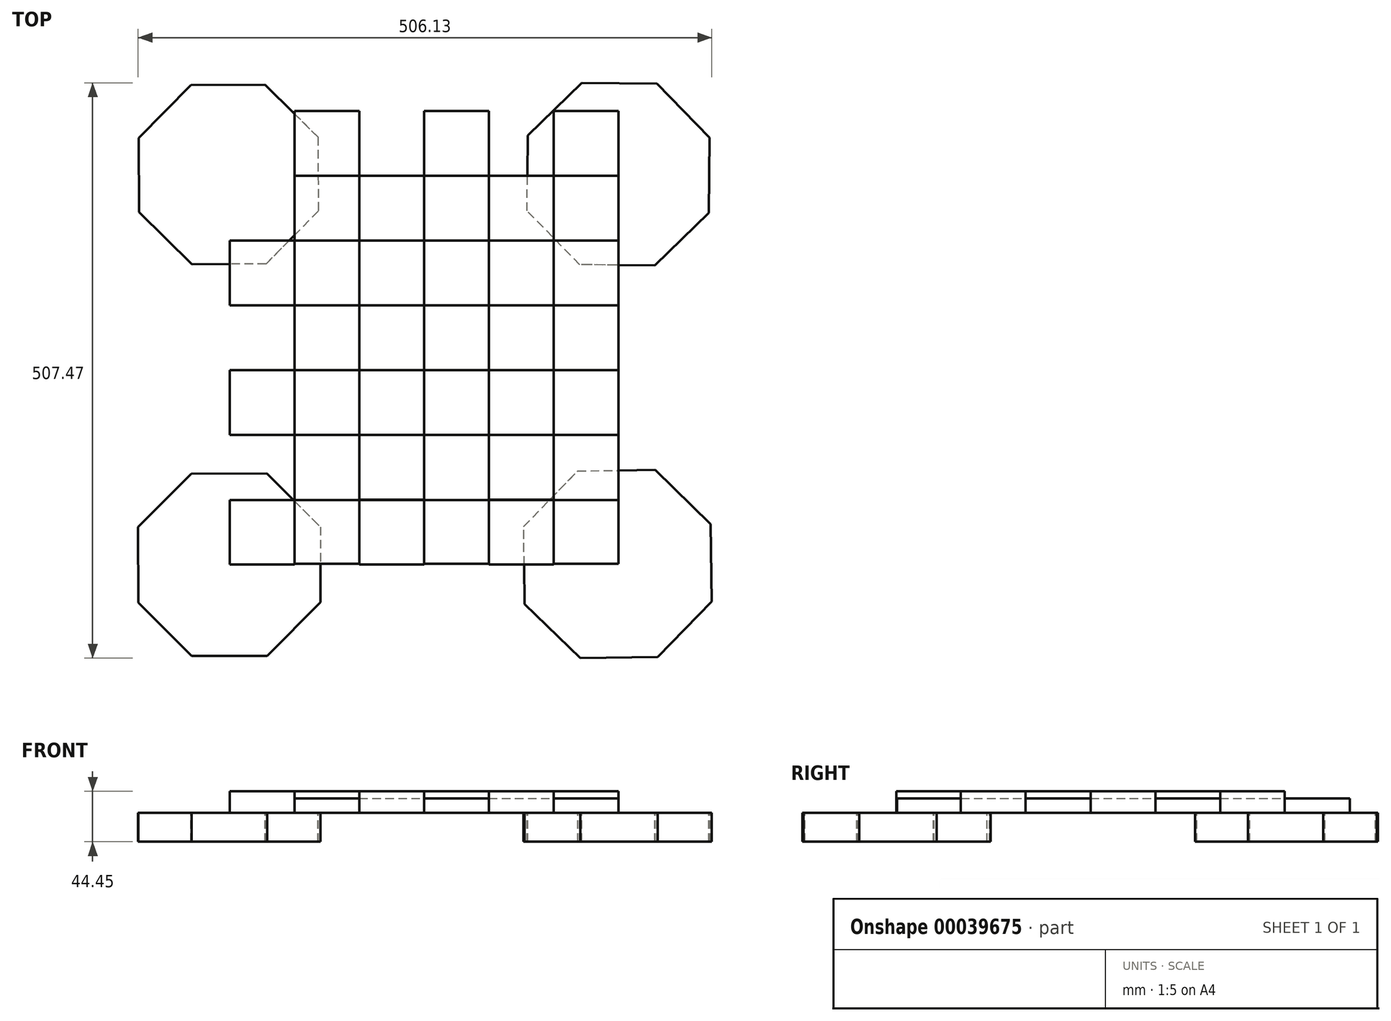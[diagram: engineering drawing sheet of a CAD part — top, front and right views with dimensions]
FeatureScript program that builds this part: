
annotation { "Feature Type Name" : "Feature", "Feature Type Description" : "" }
export const myFeature = defineFeature(function(context is Context, id is Id, definition is map)
    precondition{}
    {
        {
            var Q0;
            Q0=qCreatedBy(makeId("Top.planeOp"),FACE);
            var sketch = newSketch(context, id + "F0", { "sketchPlane" : qUnion([Q0])});
            skLineSegment(sketch, "E0.bottom", {"start": v(0, 0) * mm, "end": v(457.2, 0) * mm});
            skLineSegment(sketch, "E0.top", {"start": v(0, 457.2) * mm, "end": v(457.2, 457.2) * mm});
            skLineSegment(sketch, "E0.left", {"start": v(0, 0) * mm, "end": v(0, 457.2) * mm});
            skLineSegment(sketch, "E0.right", {"start": v(457.2, 0) * mm, "end": v(457.2, 457.2) * mm});
            skLineSegment(sketch, "E1.bottom", {"start": v(0, 457.2) * mm, "end": v(57.15, 457.2) * mm});
            skLineSegment(sketch, "E1.top", {"start": v(0, 0) * mm, "end": v(57.15, 0) * mm});
            skLineSegment(sketch, "E1.left", {"start": v(0, 457.2) * mm, "end": v(0, 0) * mm});
            skLineSegment(sketch, "E1.right", {"start": v(57.15, 457.2) * mm, "end": v(57.15, 0) * mm});
            skLineSegment(sketch, "E2.bottom", {"start": v(457.2, 457.2) * mm, "end": v(400.05, 457.2) * mm});
            skLineSegment(sketch, "E2.top", {"start": v(457.2, 0) * mm, "end": v(400.05, 0) * mm});
            skLineSegment(sketch, "E2.left", {"start": v(457.2, 457.2) * mm, "end": v(457.2, 0) * mm});
            skLineSegment(sketch, "E2.right", {"start": v(400.05, 457.2) * mm, "end": v(400.05, 0) * mm});
            skLineSegment(sketch, "E3.bottom", {"start": v(57.15, 0) * mm, "end": v(114.3, 0) * mm});
            skLineSegment(sketch, "E3.top", {"start": v(57.15, 457.2) * mm, "end": v(114.3, 457.2) * mm});
            skLineSegment(sketch, "E3.left", {"start": v(57.15, 0) * mm, "end": v(57.15, 457.2) * mm});
            skLineSegment(sketch, "E3.right", {"start": v(114.3, 0) * mm, "end": v(114.3, 457.2) * mm});
            skLineSegment(sketch, "E4.bottom", {"start": v(114.3, 0) * mm, "end": v(171.45, 0) * mm});
            skLineSegment(sketch, "E4.top", {"start": v(114.3, 457.2) * mm, "end": v(171.45, 457.2) * mm});
            skLineSegment(sketch, "E4.right", {"start": v(171.45, 0) * mm, "end": v(171.45, 457.2) * mm});
            skLineSegment(sketch, "E5.bottom", {"start": v(171.45, 0) * mm, "end": v(228.6, 0) * mm});
            skLineSegment(sketch, "E5.top", {"start": v(171.45, 457.2) * mm, "end": v(228.6, 457.2) * mm});
            skLineSegment(sketch, "E5.right", {"start": v(228.6, 0) * mm, "end": v(228.6, 457.2) * mm});
            skLineSegment(sketch, "E6.bottom", {"start": v(228.6, 0) * mm, "end": v(285.75, 0) * mm});
            skLineSegment(sketch, "E6.top", {"start": v(228.6, 457.2) * mm, "end": v(285.75, 457.2) * mm});
            skLineSegment(sketch, "E6.right", {"start": v(285.75, 0) * mm, "end": v(285.75, 457.2) * mm});
            skLineSegment(sketch, "E7.bottom", {"start": v(285.75, 0) * mm, "end": v(342.9, 0) * mm});
            skLineSegment(sketch, "E7.top", {"start": v(285.75, 457.2) * mm, "end": v(342.9, 457.2) * mm});
            skLineSegment(sketch, "E7.right", {"start": v(342.9, 0) * mm, "end": v(342.9, 457.2) * mm});
            skLineSegment(sketch, "E8.top", {"start": v(0, 400.05) * mm, "end": v(457.2, 400.05) * mm});
            skLineSegment(sketch, "E8.left", {"start": v(0, 457.2) * mm, "end": v(0, 400.05) * mm});
            skLineSegment(sketch, "E8.right", {"start": v(457.2, 457.2) * mm, "end": v(457.2, 400.05) * mm});
            skLineSegment(sketch, "E9.top", {"start": v(0, 342.9) * mm, "end": v(457.2, 342.9) * mm});
            skLineSegment(sketch, "E9.left", {"start": v(0, 400.05) * mm, "end": v(0, 342.9) * mm});
            skLineSegment(sketch, "E9.right", {"start": v(457.2, 400.05) * mm, "end": v(457.2, 342.9) * mm});
            skLineSegment(sketch, "E10.top", {"start": v(0, 285.75) * mm, "end": v(457.2, 285.75) * mm});
            skLineSegment(sketch, "E10.left", {"start": v(0, 342.9) * mm, "end": v(0, 285.75) * mm});
            skLineSegment(sketch, "E10.right", {"start": v(457.2, 342.9) * mm, "end": v(457.2, 285.75) * mm});
            skLineSegment(sketch, "E11.top", {"start": v(0, 228.6) * mm, "end": v(457.2, 228.6) * mm});
            skLineSegment(sketch, "E11.left", {"start": v(0, 285.75) * mm, "end": v(0, 228.6) * mm});
            skLineSegment(sketch, "E11.right", {"start": v(457.2, 285.75) * mm, "end": v(457.2, 228.6) * mm});
            skLineSegment(sketch, "E12.top", {"start": v(0, 171.45) * mm, "end": v(457.2, 171.45) * mm});
            skLineSegment(sketch, "E12.left", {"start": v(0, 228.6) * mm, "end": v(0, 171.45) * mm});
            skLineSegment(sketch, "E12.right", {"start": v(457.2, 228.6) * mm, "end": v(457.2, 171.45) * mm});
            skLineSegment(sketch, "E13.top", {"start": v(0, 114.3) * mm, "end": v(457.2, 114.3) * mm});
            skLineSegment(sketch, "E13.left", {"start": v(0, 171.45) * mm, "end": v(0, 114.3) * mm});
            skLineSegment(sketch, "E13.right", {"start": v(457.2, 171.45) * mm, "end": v(457.2, 114.3) * mm});
            skLineSegment(sketch, "E14.top", {"start": v(0, 57.83) * mm, "end": v(457.2, 57.83) * mm});
            skLineSegment(sketch, "E14.left", {"start": v(0, 114.3) * mm, "end": v(0, 57.83) * mm});
            skLineSegment(sketch, "E14.right", {"start": v(457.2, 114.3) * mm, "end": v(457.2, 57.83) * mm});
            skSolve(sketch);
        }
        {
            var Q0;
            {var subQ4=sQuery(id+"F0.wireOp",EDGE,"E2.top");Q0=makeQuery(id+"F0.imprint","IMPRINT",FACE,{"disambiguationData":[TD([[makeQuery(id+"F0.imprint","IMPRINT",EDGE,{"derivedFrom":subQ4}),-1.0]])]});}
            var Q1;
            {var subQ5=sQuery(id+"F0.wireOp",EDGE,"E7.bottom");Q1=makeQuery(id+"F0.imprint","IMPRINT",FACE,{"disambiguationData":[TD([[makeQuery(id+"F0.imprint","IMPRINT",EDGE,{"derivedFrom":subQ5}),1.0]])]});}
            var Q2;
            {var subQ3=sQuery(id+"F0.wireOp",EDGE,"E5.bottom");Q2=makeQuery(id+"F0.imprint","IMPRINT",FACE,{"disambiguationData":[TD([[makeQuery(id+"F0.imprint","IMPRINT",EDGE,{"derivedFrom":subQ3}),1.0]])]});}
            var Q3;
            {var subQ5=sQuery(id+"F0.wireOp",EDGE,"E3.bottom");Q3=makeQuery(id+"F0.imprint","IMPRINT",FACE,{"disambiguationData":[TD([[makeQuery(id+"F0.imprint","IMPRINT",EDGE,{"derivedFrom":subQ5}),1.0]])]});}
            var Q4;
            {var subQ0=sQuery(id+"F0.wireOp",EDGE,"E13.top");var subQ3=sQuery(id+"F0.wireOp",EDGE,"E2.right");var subQ4=makeQuery(id+"F0.imprint","INTERSECT",VERTEX,{"derivedFrom":[subQ3,subQ0]});Q4=makeQuery(id+"F0.imprint","IMPRINT",FACE,{"disambiguationData":[TD([[makeQuery(id+"F0.imprint","IMPRINT",EDGE,{"disambiguationData":[TD([[subQ4,-1.0]])],"derivedFrom":subQ3}),-1.0]])]});}
            var Q5;
            {var subQ0=sQuery(id+"F0.wireOp",EDGE,"E14.top");var subQ3=sQuery(id+"F0.wireOp",EDGE,"E5.right");var subQ4=makeQuery(id+"F0.imprint","INTERSECT",VERTEX,{"derivedFrom":[subQ3,subQ0]});Q5=makeQuery(id+"F0.imprint","IMPRINT",FACE,{"disambiguationData":[TD([[makeQuery(id+"F0.imprint","IMPRINT",EDGE,{"disambiguationData":[TD([[subQ4,-1.0]])],"derivedFrom":subQ3}),-1.0]])]});}
            var Q6;
            {var subQ0=sQuery(id+"F0.wireOp",EDGE,"E14.top");var subQ3=sQuery(id+"F0.wireOp",EDGE,"E3.right");var subQ4=makeQuery(id+"F0.imprint","INTERSECT",VERTEX,{"derivedFrom":[subQ3,subQ0]});Q6=makeQuery(id+"F0.imprint","IMPRINT",FACE,{"disambiguationData":[TD([[makeQuery(id+"F0.imprint","IMPRINT",EDGE,{"disambiguationData":[TD([[subQ4,-1.0]])],"derivedFrom":subQ3}),-1.0]])]});}
            var Q7;
            {var subQ3=sQuery(id+"F0.wireOp",EDGE,"E14.left");Q7=makeQuery(id+"F0.imprint","IMPRINT",FACE,{"disambiguationData":[TD([[makeQuery(id+"F0.imprint","IMPRINT",EDGE,{"derivedFrom":subQ3}),1.0]])]});}
            var Q8;
            {var subQ0=sQuery(id+"F0.wireOp",EDGE,"E13.top");var subQ3=sQuery(id+"F0.wireOp",EDGE,"E6.right");var subQ4=makeQuery(id+"F0.imprint","INTERSECT",VERTEX,{"derivedFrom":[subQ3,subQ0]});Q8=makeQuery(id+"F0.imprint","IMPRINT",FACE,{"disambiguationData":[TD([[makeQuery(id+"F0.imprint","IMPRINT",EDGE,{"disambiguationData":[TD([[subQ4,-1.0]])],"derivedFrom":subQ3}),-1.0]])]});}
            var Q9;
            {var subQ0=sQuery(id+"F0.wireOp",EDGE,"E13.top");var subQ3=sQuery(id+"F0.wireOp",EDGE,"E4.right");var subQ4=makeQuery(id+"F0.imprint","INTERSECT",VERTEX,{"derivedFrom":[subQ3,subQ0]});Q9=makeQuery(id+"F0.imprint","IMPRINT",FACE,{"disambiguationData":[TD([[makeQuery(id+"F0.imprint","IMPRINT",EDGE,{"disambiguationData":[TD([[subQ4,-1.0]])],"derivedFrom":subQ3}),-1.0]])]});}
            var Q10;
            {var subQ3=sQuery(id+"F0.wireOp",EDGE,"E5.right");var subQ5=sQuery(id+"F0.wireOp",EDGE,"E12.top");var subQ7=makeQuery(id+"F0.imprint","INTERSECT",VERTEX,{"derivedFrom":[subQ3,subQ5]});Q10=makeQuery(id+"F0.imprint","IMPRINT",FACE,{"disambiguationData":[TD([[makeQuery(id+"F0.imprint","IMPRINT",EDGE,{"disambiguationData":[TD([[subQ7,-1.0]])],"derivedFrom":subQ3}),-1.0]])]});}
            var Q11;
            {var subQ0=sQuery(id+"F0.wireOp",EDGE,"E11.top");var subQ3=sQuery(id+"F0.wireOp",EDGE,"E2.right");var subQ4=makeQuery(id+"F0.imprint","INTERSECT",VERTEX,{"derivedFrom":[subQ3,subQ0]});Q11=makeQuery(id+"F0.imprint","IMPRINT",FACE,{"disambiguationData":[TD([[makeQuery(id+"F0.imprint","IMPRINT",EDGE,{"disambiguationData":[TD([[subQ4,-1.0]])],"derivedFrom":subQ3}),-1.0]])]});}
            var Q12;
            {var subQ3=sQuery(id+"F0.wireOp",EDGE,"E13.right");Q12=makeQuery(id+"F0.imprint","IMPRINT",FACE,{"disambiguationData":[TD([[makeQuery(id+"F0.imprint","IMPRINT",EDGE,{"derivedFrom":subQ3}),-1.0]])]});}
            var Q13;
            {var subQ3=sQuery(id+"F0.wireOp",EDGE,"E11.right");Q13=makeQuery(id+"F0.imprint","IMPRINT",FACE,{"disambiguationData":[TD([[makeQuery(id+"F0.imprint","IMPRINT",EDGE,{"derivedFrom":subQ3}),-1.0]])]});}
            var Q14;
            {var subQ0=sQuery(id+"F0.wireOp",EDGE,"E11.top");var subQ3=sQuery(id+"F0.wireOp",EDGE,"E6.right");var subQ4=makeQuery(id+"F0.imprint","INTERSECT",VERTEX,{"derivedFrom":[subQ3,subQ0]});Q14=makeQuery(id+"F0.imprint","IMPRINT",FACE,{"disambiguationData":[TD([[makeQuery(id+"F0.imprint","IMPRINT",EDGE,{"disambiguationData":[TD([[subQ4,-1.0]])],"derivedFrom":subQ3}),-1.0]])]});}
            var Q15;
            {var subQ0=sQuery(id+"F0.wireOp",EDGE,"E11.top");var subQ3=sQuery(id+"F0.wireOp",EDGE,"E4.right");var subQ4=makeQuery(id+"F0.imprint","INTERSECT",VERTEX,{"derivedFrom":[subQ3,subQ0]});Q15=makeQuery(id+"F0.imprint","IMPRINT",FACE,{"disambiguationData":[TD([[makeQuery(id+"F0.imprint","IMPRINT",EDGE,{"disambiguationData":[TD([[subQ4,-1.0]])],"derivedFrom":subQ3}),-1.0]])]});}
            var Q16;
            {var subQ3=sQuery(id+"F0.wireOp",EDGE,"E3.right");var subQ5=sQuery(id+"F0.wireOp",EDGE,"E12.top");var subQ7=makeQuery(id+"F0.imprint","INTERSECT",VERTEX,{"derivedFrom":[subQ3,subQ5]});Q16=makeQuery(id+"F0.imprint","IMPRINT",FACE,{"disambiguationData":[TD([[makeQuery(id+"F0.imprint","IMPRINT",EDGE,{"disambiguationData":[TD([[subQ7,-1.0]])],"derivedFrom":subQ3}),-1.0]])]});}
            var Q17;
            {var subQ3=sQuery(id+"F0.wireOp",EDGE,"E12.left");Q17=makeQuery(id+"F0.imprint","IMPRINT",FACE,{"disambiguationData":[TD([[makeQuery(id+"F0.imprint","IMPRINT",EDGE,{"derivedFrom":subQ3}),1.0]])]});}
            var Q18;
            {var subQ3=sQuery(id+"F0.wireOp",EDGE,"E3.left");var subQ5=sQuery(id+"F0.wireOp",EDGE,"E13.top");var subQ7=makeQuery(id+"F0.imprint","INTERSECT",VERTEX,{"derivedFrom":[subQ3,subQ5]});Q18=makeQuery(id+"F0.imprint","IMPRINT",FACE,{"disambiguationData":[TD([[makeQuery(id+"F0.imprint","IMPRINT",EDGE,{"disambiguationData":[TD([[subQ7,-1.0]])],"derivedFrom":subQ3}),-1.0]])]});}
            var Q19;
            {var subQ0=sQuery(id+"F0.wireOp",EDGE,"E11.top");var subQ3=sQuery(id+"F0.wireOp",EDGE,"E3.left");var subQ4=makeQuery(id+"F0.imprint","INTERSECT",VERTEX,{"derivedFrom":[subQ3,subQ0]});Q19=makeQuery(id+"F0.imprint","IMPRINT",FACE,{"disambiguationData":[TD([[makeQuery(id+"F0.imprint","IMPRINT",EDGE,{"disambiguationData":[TD([[subQ4,-1.0]])],"derivedFrom":subQ3}),-1.0]])]});}
            var Q20;
            {var subQ0=sQuery(id+"F0.wireOp",EDGE,"E10.left");Q20=makeQuery(id+"F0.imprint","IMPRINT",FACE,{"disambiguationData":[TD([[makeQuery(id+"F0.imprint","IMPRINT",EDGE,{"derivedFrom":subQ0}),1.0]])]});}
            var Q21;
            {var subQ0=sQuery(id+"F0.wireOp",EDGE,"E10.top");var subQ3=sQuery(id+"F0.wireOp",EDGE,"E3.right");var subQ4=makeQuery(id+"F0.imprint","INTERSECT",VERTEX,{"derivedFrom":[subQ3,subQ0]});Q21=makeQuery(id+"F0.imprint","IMPRINT",FACE,{"disambiguationData":[TD([[makeQuery(id+"F0.imprint","IMPRINT",EDGE,{"disambiguationData":[TD([[subQ4,-1.0]])],"derivedFrom":subQ3}),-1.0]])]});}
            var Q22;
            {var subQ3=sQuery(id+"F0.wireOp",EDGE,"E5.right");var subQ5=sQuery(id+"F0.wireOp",EDGE,"E10.top");var subQ7=makeQuery(id+"F0.imprint","INTERSECT",VERTEX,{"derivedFrom":[subQ3,subQ5]});Q22=makeQuery(id+"F0.imprint","IMPRINT",FACE,{"disambiguationData":[TD([[makeQuery(id+"F0.imprint","IMPRINT",EDGE,{"disambiguationData":[TD([[subQ7,-1.0]])],"derivedFrom":subQ3}),-1.0]])]});}
            var Q23;
            {var subQ0=sQuery(id+"F0.wireOp",EDGE,"E9.top");var subQ3=sQuery(id+"F0.wireOp",EDGE,"E2.right");var subQ4=makeQuery(id+"F0.imprint","INTERSECT",VERTEX,{"derivedFrom":[subQ3,subQ0]});Q23=makeQuery(id+"F0.imprint","IMPRINT",FACE,{"disambiguationData":[TD([[makeQuery(id+"F0.imprint","IMPRINT",EDGE,{"disambiguationData":[TD([[subQ4,-1.0]])],"derivedFrom":subQ3}),-1.0]])]});}
            var Q24;
            {var subQ3=sQuery(id+"F0.wireOp",EDGE,"E9.right");Q24=makeQuery(id+"F0.imprint","IMPRINT",FACE,{"disambiguationData":[TD([[makeQuery(id+"F0.imprint","IMPRINT",EDGE,{"derivedFrom":subQ3}),-1.0]])]});}
            var Q25;
            {var subQ0=sQuery(id+"F0.wireOp",EDGE,"E9.top");var subQ3=sQuery(id+"F0.wireOp",EDGE,"E6.right");var subQ4=makeQuery(id+"F0.imprint","INTERSECT",VERTEX,{"derivedFrom":[subQ3,subQ0]});Q25=makeQuery(id+"F0.imprint","IMPRINT",FACE,{"disambiguationData":[TD([[makeQuery(id+"F0.imprint","IMPRINT",EDGE,{"disambiguationData":[TD([[subQ4,-1.0]])],"derivedFrom":subQ3}),-1.0]])]});}
            var Q26;
            {var subQ0=sQuery(id+"F0.wireOp",EDGE,"E9.top");var subQ3=sQuery(id+"F0.wireOp",EDGE,"E4.right");var subQ4=makeQuery(id+"F0.imprint","INTERSECT",VERTEX,{"derivedFrom":[subQ3,subQ0]});Q26=makeQuery(id+"F0.imprint","IMPRINT",FACE,{"disambiguationData":[TD([[makeQuery(id+"F0.imprint","IMPRINT",EDGE,{"disambiguationData":[TD([[subQ4,-1.0]])],"derivedFrom":subQ3}),-1.0]])]});}
            var Q27;
            {var subQ3=sQuery(id+"F0.wireOp",EDGE,"E3.left");var subQ5=sQuery(id+"F0.wireOp",EDGE,"E9.top");var subQ7=makeQuery(id+"F0.imprint","INTERSECT",VERTEX,{"derivedFrom":[subQ3,subQ5]});Q27=makeQuery(id+"F0.imprint","IMPRINT",FACE,{"disambiguationData":[TD([[makeQuery(id+"F0.imprint","IMPRINT",EDGE,{"disambiguationData":[TD([[subQ7,-1.0]])],"derivedFrom":subQ3}),-1.0]])]});}
            var Q28;
            {var subQ3=sQuery(id+"F0.wireOp",EDGE,"E3.right");var subQ5=sQuery(id+"F0.wireOp",EDGE,"E0.top");var subQ7=makeQuery(id+"F0.imprint","INTERSECT",VERTEX,{"derivedFrom":[subQ3,subQ5]});Q28=makeQuery(id+"F0.imprint","IMPRINT",FACE,{"disambiguationData":[TD([[makeQuery(id+"F0.imprint","IMPRINT",EDGE,{"disambiguationData":[TD([[subQ7,1.0]])],"derivedFrom":subQ3}),-1.0]])]});}
            var Q29;
            {var subQ3=sQuery(id+"F0.wireOp",EDGE,"E5.right");var subQ5=sQuery(id+"F0.wireOp",EDGE,"E0.top");var subQ7=makeQuery(id+"F0.imprint","INTERSECT",VERTEX,{"derivedFrom":[subQ3,subQ5]});Q29=makeQuery(id+"F0.imprint","IMPRINT",FACE,{"disambiguationData":[TD([[makeQuery(id+"F0.imprint","IMPRINT",EDGE,{"disambiguationData":[TD([[subQ7,1.0]])],"derivedFrom":subQ3}),-1.0]])]});}
            var Q30;
            {var subQ0=sQuery(id+"F0.wireOp",EDGE,"E0.top");var subQ3=sQuery(id+"F0.wireOp",EDGE,"E2.right");var subQ4=makeQuery(id+"F0.imprint","INTERSECT",VERTEX,{"derivedFrom":[subQ3,subQ0]});Q30=makeQuery(id+"F0.imprint","IMPRINT",FACE,{"disambiguationData":[TD([[makeQuery(id+"F0.imprint","IMPRINT",EDGE,{"disambiguationData":[TD([[subQ4,-1.0]])],"derivedFrom":subQ3}),-1.0]])]});}
            var Q31;
            {var subQ3=sQuery(id+"F0.wireOp",EDGE,"E8.left");Q31=makeQuery(id+"F0.imprint","IMPRINT",FACE,{"disambiguationData":[TD([[makeQuery(id+"F0.imprint","IMPRINT",EDGE,{"derivedFrom":subQ3}),1.0]])]});}
            extrude(context, id + "F1", {"entities" : qUnion([Q0, Q1, Q2, Q3, Q4, Q5, Q6, Q7, Q8, Q9, Q10, Q11, Q12, Q13, Q14, Q15, Q16, Q17, Q18, Q19, Q20, Q21, Q22, Q23, Q24, Q25, Q26, Q27, Q28, Q29, Q30, Q31]), "depth" : 12.7 * mm});
        }
        {
            var Q0;
            Q0=qCreatedBy(makeId("Top.planeOp"),FACE);
            var sketch = newSketch(context, id + "F2", { "sketchPlane" : qUnion([Q0])});
            skLineSegment(sketch, "E15.bottom", {"start": v(0, 0) * mm, "end": v(457.2, 0) * mm});
            skLineSegment(sketch, "E15.top", {"start": v(0, 457.2) * mm, "end": v(457.2, 457.2) * mm});
            skLineSegment(sketch, "E15.left", {"start": v(0, 0) * mm, "end": v(0, 457.2) * mm});
            skLineSegment(sketch, "E15.right", {"start": v(457.2, 0) * mm, "end": v(457.2, 457.2) * mm});
            skLineSegment(sketch, "E16.bottom", {"start": v(0, 0) * mm, "end": v(400.05, 0) * mm});
            skLineSegment(sketch, "E16.top", {"start": v(0, 400.05) * mm, "end": v(400.05, 400.05) * mm});
            skLineSegment(sketch, "E16.left", {"start": v(0, 0) * mm, "end": v(0, 400.05) * mm});
            skLineSegment(sketch, "E16.right", {"start": v(400.05, 0) * mm, "end": v(400.05, 400.05) * mm});
            skLineSegment(sketch, "E17.bottom", {"start": v(0, 0) * mm, "end": v(342.9, 0) * mm});
            skLineSegment(sketch, "E17.top", {"start": v(0, 342.9) * mm, "end": v(342.9, 342.9) * mm});
            skLineSegment(sketch, "E17.left", {"start": v(0, 0) * mm, "end": v(0, 342.9) * mm});
            skLineSegment(sketch, "E17.right", {"start": v(342.9, 0) * mm, "end": v(342.9, 342.9) * mm});
            skLineSegment(sketch, "E18.bottom", {"start": v(0, 0) * mm, "end": v(285.75, 0) * mm});
            skLineSegment(sketch, "E18.top", {"start": v(0, 285.75) * mm, "end": v(285.75, 285.75) * mm});
            skLineSegment(sketch, "E18.left", {"start": v(0, 0) * mm, "end": v(0, 285.75) * mm});
            skLineSegment(sketch, "E18.right", {"start": v(285.75, 0) * mm, "end": v(285.75, 285.75) * mm});
            skLineSegment(sketch, "E19.bottom", {"start": v(0, 0) * mm, "end": v(228.6, 0) * mm});
            skLineSegment(sketch, "E19.top", {"start": v(0, 228.6) * mm, "end": v(228.6, 228.6) * mm});
            skLineSegment(sketch, "E19.left", {"start": v(0, 0) * mm, "end": v(0, 228.6) * mm});
            skLineSegment(sketch, "E19.right", {"start": v(228.6, 0) * mm, "end": v(228.6, 228.6) * mm});
            skLineSegment(sketch, "E20.bottom", {"start": v(0, 0) * mm, "end": v(171.45, 0) * mm});
            skLineSegment(sketch, "E20.top", {"start": v(0, 171.45) * mm, "end": v(171.45, 171.45) * mm});
            skLineSegment(sketch, "E20.left", {"start": v(0, 0) * mm, "end": v(0, 171.45) * mm});
            skLineSegment(sketch, "E20.right", {"start": v(171.45, 0) * mm, "end": v(171.45, 171.45) * mm});
            skLineSegment(sketch, "E21.bottom", {"start": v(0, 0) * mm, "end": v(114.3, 0) * mm});
            skLineSegment(sketch, "E21.top", {"start": v(0, 114) * mm, "end": v(114.3, 114) * mm});
            skLineSegment(sketch, "E21.left", {"start": v(0, 0) * mm, "end": v(0, 114) * mm});
            skLineSegment(sketch, "E21.right", {"start": v(114.3, 0) * mm, "end": v(114.3, 114) * mm});
            skLineSegment(sketch, "E22.bottom", {"start": v(0, 0) * mm, "end": v(57.15, 0) * mm});
            skLineSegment(sketch, "E22.top", {"start": v(0, 57.15) * mm, "end": v(57.15, 57.15) * mm});
            skLineSegment(sketch, "E22.left", {"start": v(0, 0) * mm, "end": v(0, 57.15) * mm});
            skLineSegment(sketch, "E22.right", {"start": v(57.15, 0) * mm, "end": v(57.15, 57.15) * mm});
            skLineSegment(sketch, "E23.bottom", {"start": v(457.2, 457.2) * mm, "end": v(57.15, 457.2) * mm});
            skLineSegment(sketch, "E23.top", {"start": v(457.2, 57.15) * mm, "end": v(57.15, 57.15) * mm});
            skLineSegment(sketch, "E23.left", {"start": v(457.2, 457.2) * mm, "end": v(457.2, 57.15) * mm});
            skLineSegment(sketch, "E23.right", {"start": v(57.15, 457.2) * mm, "end": v(57.15, 57.15) * mm});
            skLineSegment(sketch, "E24.bottom", {"start": v(457.2, 457.2) * mm, "end": v(114.3, 457.2) * mm});
            skLineSegment(sketch, "E24.top", {"start": v(457.2, 114) * mm, "end": v(114.3, 114) * mm});
            skLineSegment(sketch, "E24.left", {"start": v(457.2, 457.2) * mm, "end": v(457.2, 114) * mm});
            skLineSegment(sketch, "E24.right", {"start": v(114.3, 457.2) * mm, "end": v(114.3, 114) * mm});
            skLineSegment(sketch, "E25.bottom", {"start": v(457.2, 457.2) * mm, "end": v(171.45, 457.2) * mm});
            skLineSegment(sketch, "E25.top", {"start": v(457.2, 171.45) * mm, "end": v(171.45, 171.45) * mm});
            skLineSegment(sketch, "E25.left", {"start": v(457.2, 457.2) * mm, "end": v(457.2, 171.45) * mm});
            skLineSegment(sketch, "E25.right", {"start": v(171.45, 457.2) * mm, "end": v(171.45, 171.45) * mm});
            skLineSegment(sketch, "E26.bottom", {"start": v(457.2, 457.2) * mm, "end": v(228.6, 457.2) * mm});
            skLineSegment(sketch, "E26.top", {"start": v(457.2, 228.6) * mm, "end": v(228.6, 228.6) * mm});
            skLineSegment(sketch, "E26.left", {"start": v(457.2, 457.2) * mm, "end": v(457.2, 228.6) * mm});
            skLineSegment(sketch, "E26.right", {"start": v(228.6, 457.2) * mm, "end": v(228.6, 228.6) * mm});
            skLineSegment(sketch, "E27.bottom", {"start": v(457.2, 457.2) * mm, "end": v(285.75, 457.2) * mm});
            skLineSegment(sketch, "E27.top", {"start": v(457.2, 285.75) * mm, "end": v(285.75, 285.75) * mm});
            skLineSegment(sketch, "E27.left", {"start": v(457.2, 457.2) * mm, "end": v(457.2, 285.75) * mm});
            skLineSegment(sketch, "E27.right", {"start": v(285.75, 457.2) * mm, "end": v(285.75, 285.75) * mm});
            skLineSegment(sketch, "E28.bottom", {"start": v(457.2, 457.2) * mm, "end": v(342.9, 457.2) * mm});
            skLineSegment(sketch, "E28.top", {"start": v(457.2, 342.9) * mm, "end": v(342.9, 342.9) * mm});
            skLineSegment(sketch, "E28.left", {"start": v(457.2, 457.2) * mm, "end": v(457.2, 342.9) * mm});
            skLineSegment(sketch, "E28.right", {"start": v(342.9, 457.2) * mm, "end": v(342.9, 342.9) * mm});
            skLineSegment(sketch, "E29.bottom", {"start": v(457.2, 457.2) * mm, "end": v(400.05, 457.2) * mm});
            skLineSegment(sketch, "E29.top", {"start": v(457.2, 400.05) * mm, "end": v(400.05, 400.05) * mm});
            skLineSegment(sketch, "E29.left", {"start": v(457.2, 457.2) * mm, "end": v(457.2, 400.05) * mm});
            skLineSegment(sketch, "E29.right", {"start": v(400.05, 457.2) * mm, "end": v(400.05, 400.05) * mm});
            skSolve(sketch);
        }
        {
            var Q0;
            Q0=makeQuery(id+"F2.imprint","IMPRINT",FACE,{"disambiguationData":[TD([[makeQuery(id+"F2.imprint","IMPRINT",EDGE,{"derivedFrom":sQuery(id+"F2.wireOp",EDGE,"E22.bottom")}),1.0]])]});
            var Q1;
            Q1=makeQuery(id+"F2.imprint","IMPRINT",FACE,{"disambiguationData":[TD([[makeQuery(id+"F2.imprint","IMPRINT",EDGE,{"derivedFrom":sQuery(id+"F2.wireOp",EDGE,"E29.bottom")}),1.0]])]});
            var Q2;
            {var subQ5=sQuery(id+"F2.wireOp",EDGE,"E16.bottom");Q2=makeQuery(id+"F2.imprint","IMPRINT",FACE,{"disambiguationData":[TD([[makeQuery(id+"F2.imprint","IMPRINT",EDGE,{"derivedFrom":subQ5}),1.0]])]});}
            var Q3;
            {var subQ5=sQuery(id+"F2.wireOp",EDGE,"E16.left");Q3=makeQuery(id+"F2.imprint","IMPRINT",FACE,{"disambiguationData":[TD([[makeQuery(id+"F2.imprint","IMPRINT",EDGE,{"derivedFrom":subQ5}),-1.0]])]});}
            var Q4;
            {var subQ3=sQuery(id+"F2.wireOp",EDGE,"E23.bottom");Q4=makeQuery(id+"F2.imprint","IMPRINT",FACE,{"disambiguationData":[TD([[makeQuery(id+"F2.imprint","IMPRINT",EDGE,{"derivedFrom":subQ3}),1.0]])]});}
            var Q5;
            {var subQ3=sQuery(id+"F2.wireOp",EDGE,"E25.bottom");Q5=makeQuery(id+"F2.imprint","IMPRINT",FACE,{"disambiguationData":[TD([[makeQuery(id+"F2.imprint","IMPRINT",EDGE,{"derivedFrom":subQ3}),1.0]])]});}
            var Q6;
            {var subQ3=sQuery(id+"F2.wireOp",EDGE,"E27.bottom");Q6=makeQuery(id+"F2.imprint","IMPRINT",FACE,{"disambiguationData":[TD([[makeQuery(id+"F2.imprint","IMPRINT",EDGE,{"derivedFrom":subQ3}),1.0]])]});}
            var Q7;
            {var subQ3=sQuery(id+"F2.wireOp",EDGE,"E23.left");Q7=makeQuery(id+"F2.imprint","IMPRINT",FACE,{"disambiguationData":[TD([[makeQuery(id+"F2.imprint","IMPRINT",EDGE,{"derivedFrom":subQ3}),-1.0]])]});}
            var Q8;
            {var subQ0=sQuery(id+"F2.wireOp",EDGE,"E25.left");Q8=makeQuery(id+"F2.imprint","IMPRINT",FACE,{"disambiguationData":[TD([[makeQuery(id+"F2.imprint","IMPRINT",EDGE,{"derivedFrom":subQ0}),-1.0]])]});}
            var Q9;
            {var subQ5=sQuery(id+"F2.wireOp",EDGE,"E18.bottom");Q9=makeQuery(id+"F2.imprint","IMPRINT",FACE,{"disambiguationData":[TD([[makeQuery(id+"F2.imprint","IMPRINT",EDGE,{"derivedFrom":subQ5}),1.0]])]});}
            var Q10;
            {var subQ5=sQuery(id+"F2.wireOp",EDGE,"E18.left");Q10=makeQuery(id+"F2.imprint","IMPRINT",FACE,{"disambiguationData":[TD([[makeQuery(id+"F2.imprint","IMPRINT",EDGE,{"derivedFrom":subQ5}),-1.0]])]});}
            var Q11;
            {var subQ5=sQuery(id+"F2.wireOp",EDGE,"E20.bottom");Q11=makeQuery(id+"F2.imprint","IMPRINT",FACE,{"disambiguationData":[TD([[makeQuery(id+"F2.imprint","IMPRINT",EDGE,{"derivedFrom":subQ5}),1.0]])]});}
            var Q12;
            {var subQ5=sQuery(id+"F2.wireOp",EDGE,"E20.left");Q12=makeQuery(id+"F2.imprint","IMPRINT",FACE,{"disambiguationData":[TD([[makeQuery(id+"F2.imprint","IMPRINT",EDGE,{"derivedFrom":subQ5}),-1.0]])]});}
            var Q13;
            {var subQ0=sQuery(id+"F2.wireOp",EDGE,"E26.top");var subQ3=sQuery(id+"F2.wireOp",EDGE,"E16.right");var subQ4=makeQuery(id+"F2.imprint","INTERSECT",VERTEX,{"derivedFrom":[subQ3,subQ0]});Q13=makeQuery(id+"F2.imprint","IMPRINT",FACE,{"disambiguationData":[TD([[makeQuery(id+"F2.imprint","IMPRINT",EDGE,{"disambiguationData":[TD([[subQ4,-1.0]])],"derivedFrom":subQ3}),1.0]])]});}
            var Q14;
            {var subQ0=sQuery(id+"F2.wireOp",EDGE,"E27.right");var subQ1=sQuery(id+"F2.wireOp",EDGE,"E17.top");var subQ2=makeQuery(id+"F2.imprint","INTERSECT",VERTEX,{"derivedFrom":[subQ1,subQ0]});Q14=makeQuery(id+"F2.imprint","IMPRINT",FACE,{"disambiguationData":[TD([[makeQuery(id+"F2.imprint","IMPRINT",EDGE,{"disambiguationData":[TD([[subQ2,-1.0]])],"derivedFrom":subQ1}),-1.0]])]});}
            var Q15;
            {var subQ3=sQuery(id+"F2.wireOp",EDGE,"E17.right");var subQ5=sQuery(id+"F2.wireOp",EDGE,"E25.top");var subQ7=makeQuery(id+"F2.imprint","INTERSECT",VERTEX,{"derivedFrom":[subQ3,subQ5]});Q15=makeQuery(id+"F2.imprint","IMPRINT",FACE,{"disambiguationData":[TD([[makeQuery(id+"F2.imprint","IMPRINT",EDGE,{"disambiguationData":[TD([[subQ7,-1.0]])],"derivedFrom":subQ3}),1.0]])]});}
            var Q16;
            {var subQ0=sQuery(id+"F2.wireOp",EDGE,"E28.right");var subQ1=sQuery(id+"F2.wireOp",EDGE,"E16.top");var subQ2=makeQuery(id+"F2.imprint","INTERSECT",VERTEX,{"derivedFrom":[subQ1,subQ0]});Q16=makeQuery(id+"F2.imprint","IMPRINT",FACE,{"disambiguationData":[TD([[makeQuery(id+"F2.imprint","IMPRINT",EDGE,{"disambiguationData":[TD([[subQ2,-1.0]])],"derivedFrom":subQ1}),-1.0]])]});}
            var Q17;
            {var subQ3=sQuery(id+"F2.wireOp",EDGE,"E27.left");Q17=makeQuery(id+"F2.imprint","IMPRINT",FACE,{"disambiguationData":[TD([[makeQuery(id+"F2.imprint","IMPRINT",EDGE,{"derivedFrom":subQ3}),-1.0]])]});}
            var Q18;
            {var subQ3=sQuery(id+"F2.wireOp",EDGE,"E16.right");var subQ5=sQuery(id+"F2.wireOp",EDGE,"E24.top");var subQ7=makeQuery(id+"F2.imprint","INTERSECT",VERTEX,{"derivedFrom":[subQ3,subQ5]});Q18=makeQuery(id+"F2.imprint","IMPRINT",FACE,{"disambiguationData":[TD([[makeQuery(id+"F2.imprint","IMPRINT",EDGE,{"disambiguationData":[TD([[subQ7,-1.0]])],"derivedFrom":subQ3}),1.0]])]});}
            var Q19;
            {var subQ3=sQuery(id+"F2.wireOp",EDGE,"E23.top");var subQ5=sQuery(id+"F2.wireOp",EDGE,"E17.right");var subQ7=makeQuery(id+"F2.imprint","INTERSECT",VERTEX,{"derivedFrom":[subQ5,subQ3]});Q19=makeQuery(id+"F2.imprint","IMPRINT",FACE,{"disambiguationData":[TD([[makeQuery(id+"F2.imprint","IMPRINT",EDGE,{"disambiguationData":[TD([[subQ7,-1.0]])],"derivedFrom":subQ5}),1.0]])]});}
            var Q20;
            {var subQ3=sQuery(id+"F2.wireOp",EDGE,"E18.right");var subQ5=sQuery(id+"F2.wireOp",EDGE,"E24.top");var subQ7=makeQuery(id+"F2.imprint","INTERSECT",VERTEX,{"derivedFrom":[subQ3,subQ5]});Q20=makeQuery(id+"F2.imprint","IMPRINT",FACE,{"disambiguationData":[TD([[makeQuery(id+"F2.imprint","IMPRINT",EDGE,{"disambiguationData":[TD([[subQ7,-1.0]])],"derivedFrom":subQ3}),1.0]])]});}
            var Q21;
            {var subQ0=sQuery(id+"F2.wireOp",EDGE,"E23.top");var subQ3=sQuery(id+"F2.wireOp",EDGE,"E19.right");var subQ4=makeQuery(id+"F2.imprint","INTERSECT",VERTEX,{"derivedFrom":[subQ3,subQ0]});Q21=makeQuery(id+"F2.imprint","IMPRINT",FACE,{"disambiguationData":[TD([[makeQuery(id+"F2.imprint","IMPRINT",EDGE,{"disambiguationData":[TD([[subQ4,-1.0]])],"derivedFrom":subQ3}),1.0]])]});}
            var Q22;
            {var subQ3=sQuery(id+"F2.wireOp",EDGE,"E25.right");var subQ5=sQuery(id+"F2.wireOp",EDGE,"E19.top");var subQ6=makeQuery(id+"F2.imprint","INTERSECT",VERTEX,{"derivedFrom":[subQ5,subQ3]});Q22=makeQuery(id+"F2.imprint","IMPRINT",FACE,{"disambiguationData":[TD([[makeQuery(id+"F2.imprint","IMPRINT",EDGE,{"disambiguationData":[TD([[subQ6,-1.0]])],"derivedFrom":subQ5}),-1.0]])]});}
            var Q23;
            {var subQ0=sQuery(id+"F2.wireOp",EDGE,"E26.right");var subQ1=sQuery(id+"F2.wireOp",EDGE,"E18.top");var subQ2=makeQuery(id+"F2.imprint","INTERSECT",VERTEX,{"derivedFrom":[subQ1,subQ0]});Q23=makeQuery(id+"F2.imprint","IMPRINT",FACE,{"disambiguationData":[TD([[makeQuery(id+"F2.imprint","IMPRINT",EDGE,{"disambiguationData":[TD([[subQ2,-1.0]])],"derivedFrom":subQ1}),-1.0]])]});}
            var Q24;
            {var subQ3=sQuery(id+"F2.wireOp",EDGE,"E16.top");var subQ5=sQuery(id+"F2.wireOp",EDGE,"E26.right");var subQ7=makeQuery(id+"F2.imprint","INTERSECT",VERTEX,{"derivedFrom":[subQ3,subQ5]});Q24=makeQuery(id+"F2.imprint","IMPRINT",FACE,{"disambiguationData":[TD([[makeQuery(id+"F2.imprint","IMPRINT",EDGE,{"disambiguationData":[TD([[subQ7,-1.0]])],"derivedFrom":subQ3}),-1.0]])]});}
            var Q25;
            {var subQ0=sQuery(id+"F2.wireOp",EDGE,"E24.right");var subQ3=sQuery(id+"F2.wireOp",EDGE,"E16.top");var subQ4=makeQuery(id+"F2.imprint","INTERSECT",VERTEX,{"derivedFrom":[subQ3,subQ0]});Q25=makeQuery(id+"F2.imprint","IMPRINT",FACE,{"disambiguationData":[TD([[makeQuery(id+"F2.imprint","IMPRINT",EDGE,{"disambiguationData":[TD([[subQ4,-1.0]])],"derivedFrom":subQ3}),-1.0]])]});}
            var Q26;
            {var subQ3=sQuery(id+"F2.wireOp",EDGE,"E17.top");var subQ5=sQuery(id+"F2.wireOp",EDGE,"E25.right");var subQ7=makeQuery(id+"F2.imprint","INTERSECT",VERTEX,{"derivedFrom":[subQ3,subQ5]});Q26=makeQuery(id+"F2.imprint","IMPRINT",FACE,{"disambiguationData":[TD([[makeQuery(id+"F2.imprint","IMPRINT",EDGE,{"disambiguationData":[TD([[subQ7,-1.0]])],"derivedFrom":subQ3}),-1.0]])]});}
            var Q27;
            {var subQ3=sQuery(id+"F2.wireOp",EDGE,"E17.top");var subQ5=sQuery(id+"F2.wireOp",EDGE,"E23.right");var subQ7=makeQuery(id+"F2.imprint","INTERSECT",VERTEX,{"derivedFrom":[subQ3,subQ5]});Q27=makeQuery(id+"F2.imprint","IMPRINT",FACE,{"disambiguationData":[TD([[makeQuery(id+"F2.imprint","IMPRINT",EDGE,{"disambiguationData":[TD([[subQ7,-1.0]])],"derivedFrom":subQ3}),-1.0]])]});}
            var Q28;
            {var subQ3=sQuery(id+"F2.wireOp",EDGE,"E18.top");var subQ5=sQuery(id+"F2.wireOp",EDGE,"E24.right");var subQ7=makeQuery(id+"F2.imprint","INTERSECT",VERTEX,{"derivedFrom":[subQ3,subQ5]});Q28=makeQuery(id+"F2.imprint","IMPRINT",FACE,{"disambiguationData":[TD([[makeQuery(id+"F2.imprint","IMPRINT",EDGE,{"disambiguationData":[TD([[subQ7,-1.0]])],"derivedFrom":subQ3}),-1.0]])]});}
            var Q29;
            {var subQ3=sQuery(id+"F2.wireOp",EDGE,"E19.top");var subQ5=sQuery(id+"F2.wireOp",EDGE,"E23.right");var subQ7=makeQuery(id+"F2.imprint","INTERSECT",VERTEX,{"derivedFrom":[subQ3,subQ5]});Q29=makeQuery(id+"F2.imprint","IMPRINT",FACE,{"disambiguationData":[TD([[makeQuery(id+"F2.imprint","IMPRINT",EDGE,{"disambiguationData":[TD([[subQ7,-1.0]])],"derivedFrom":subQ3}),-1.0]])]});}
            var Q30;
            {var subQ3=sQuery(id+"F2.wireOp",EDGE,"E24.right");var subQ5=sQuery(id+"F2.wireOp",EDGE,"E20.top");var subQ6=makeQuery(id+"F2.imprint","INTERSECT",VERTEX,{"derivedFrom":[subQ5,subQ3]});Q30=makeQuery(id+"F2.imprint","IMPRINT",FACE,{"disambiguationData":[TD([[makeQuery(id+"F2.imprint","IMPRINT",EDGE,{"disambiguationData":[TD([[subQ6,-1.0]])],"derivedFrom":subQ5}),-1.0]])]});}
            var Q31;
            {var subQ0=sQuery(id+"F2.wireOp",EDGE,"E23.right");var subQ1=sQuery(id+"F2.wireOp",EDGE,"E21.top");var subQ2=makeQuery(id+"F2.imprint","INTERSECT",VERTEX,{"derivedFrom":[subQ1,subQ0]});Q31=makeQuery(id+"F2.imprint","IMPRINT",FACE,{"disambiguationData":[TD([[makeQuery(id+"F2.imprint","IMPRINT",EDGE,{"disambiguationData":[TD([[subQ2,-1.0]])],"derivedFrom":subQ1}),-1.0]])]});}
            extrude(context, id + "F3", {"entities" : qUnion([Q0, Q1, Q2, Q3, Q4, Q5, Q6, Q7, Q8, Q9, Q10, Q11, Q12, Q13, Q14, Q15, Q16, Q17, Q18, Q19, Q20, Q21, Q22, Q23, Q24, Q25, Q26, Q27, Q28, Q29, Q30, Q31]), "depth" : 19.05 * mm});
        }
        {
            var Q0;
            Q0=qCreatedBy(makeId("Top.planeOp"),FACE);
            var sketch = newSketch(context, id + "F4", { "sketchPlane" : qUnion([Q0])});
            skCircle(sketch, "E30.cCircle", {"center": v(399.92, 401.49) * mm, "radius": 80.17 * mm, "construction": true});
            skLineSegment(sketch, "E30.0", {"start": v(434.02, 481.29) * mm, "end": v(480.46, 433.8) * mm});
            skLineSegment(sketch, "E30.1", {"start": v(480.46, 433.8) * mm, "end": v(479.72, 367.4) * mm});
            skLineSegment(sketch, "E30.2", {"start": v(479.72, 367.4) * mm, "end": v(432.24, 320.95) * mm});
            skLineSegment(sketch, "E30.3", {"start": v(432.24, 320.95) * mm, "end": v(365.83, 321.7) * mm});
            skLineSegment(sketch, "E30.4", {"start": v(365.83, 321.7) * mm, "end": v(319.39, 369.17) * mm});
            skLineSegment(sketch, "E30.5", {"start": v(319.39, 369.17) * mm, "end": v(320.12, 435.58) * mm});
            skLineSegment(sketch, "E30.6", {"start": v(320.12, 435.58) * mm, "end": v(367.6, 482.02) * mm});
            skLineSegment(sketch, "E30.7", {"start": v(367.6, 482.02) * mm, "end": v(434.02, 481.29) * mm});
            skPoint(sketch, "E30.0.midPoint", {"position": v(457.24, 457.55) * mm});
            skCircle(sketch, "E31.cCircle", {"center": v(56.76, 56.93) * mm, "radius": 80.39 * mm, "construction": true});
            skLineSegment(sketch, "E31.0", {"start": v(23.58, -23.51) * mm, "end": v(-23.58, 23.51) * mm});
            skLineSegment(sketch, "E31.1", {"start": v(-23.58, 23.51) * mm, "end": v(-23.68, 90.1) * mm});
            skLineSegment(sketch, "E31.2", {"start": v(-23.68, 90.1) * mm, "end": v(23.34, 137.27) * mm});
            skLineSegment(sketch, "E31.3", {"start": v(23.34, 137.27) * mm, "end": v(89.94, 137.36) * mm});
            skLineSegment(sketch, "E31.4", {"start": v(89.94, 137.36) * mm, "end": v(137.1, 90.34) * mm});
            skLineSegment(sketch, "E31.5", {"start": v(137.1, 90.34) * mm, "end": v(137.2, 23.75) * mm});
            skLineSegment(sketch, "E31.6", {"start": v(137.2, 23.75) * mm, "end": v(90.18, -23.41) * mm});
            skLineSegment(sketch, "E31.7", {"start": v(90.18, -23.41) * mm, "end": v(23.58, -23.51) * mm});
            skPoint(sketch, "E31.0.midPoint", {"position": v(0, 0) * mm});
            skCircle(sketch, "E32.cCircle", {"center": v(399.43, 57.57) * mm, "radius": 82.56 * mm, "construction": true});
            skLineSegment(sketch, "E32.0", {"start": v(482.45, 24.51) * mm, "end": v(434.76, -24.51) * mm});
            skLineSegment(sketch, "E32.1", {"start": v(434.76, -24.51) * mm, "end": v(366.37, -25.45) * mm});
            skLineSegment(sketch, "E32.2", {"start": v(366.37, -25.45) * mm, "end": v(317.35, 22.24) * mm});
            skLineSegment(sketch, "E32.3", {"start": v(317.35, 22.24) * mm, "end": v(316.4, 90.63) * mm});
            skLineSegment(sketch, "E32.4", {"start": v(316.4, 90.63) * mm, "end": v(364.1, 139.65) * mm});
            skLineSegment(sketch, "E32.5", {"start": v(364.1, 139.65) * mm, "end": v(432.48, 140.59) * mm});
            skLineSegment(sketch, "E32.6", {"start": v(432.48, 140.59) * mm, "end": v(481.5, 92.9) * mm});
            skLineSegment(sketch, "E32.7", {"start": v(481.5, 92.9) * mm, "end": v(482.45, 24.51) * mm});
            skPoint(sketch, "E32.0.midPoint", {"position": v(458.6, 0) * mm});
            skCircle(sketch, "E33.cCircle", {"center": v(56.13, 401.18) * mm, "radius": 78.99 * mm, "construction": true});
            skLineSegment(sketch, "E33.0", {"start": v(-23.02, 433.5) * mm, "end": v(23.02, 480) * mm});
            skLineSegment(sketch, "E33.1", {"start": v(23.02, 480) * mm, "end": v(88.45, 480.33) * mm});
            skLineSegment(sketch, "E33.2", {"start": v(88.45, 480.33) * mm, "end": v(134.95, 434.3) * mm});
            skLineSegment(sketch, "E33.3", {"start": v(134.95, 434.3) * mm, "end": v(135.28, 368.86) * mm});
            skLineSegment(sketch, "E33.4", {"start": v(135.28, 368.86) * mm, "end": v(89.24, 322.36) * mm});
            skLineSegment(sketch, "E33.5", {"start": v(89.24, 322.36) * mm, "end": v(23.8, 322.04) * mm});
            skLineSegment(sketch, "E33.6", {"start": v(23.8, 322.04) * mm, "end": v(-22.7, 368.07) * mm});
            skLineSegment(sketch, "E33.7", {"start": v(-22.7, 368.07) * mm, "end": v(-23.02, 433.5) * mm});
            skPoint(sketch, "E33.0.midPoint", {"position": v(0, 456.76) * mm});
            skSolve(sketch);
        }
        {
            var Q0;
            Q0=makeQuery(id+"F4.imprint","IMPRINT",FACE,{"disambiguationData":[TD([[makeQuery(id+"F4.imprint","IMPRINT",EDGE,{"derivedFrom":sQuery(id+"F4.wireOp",EDGE,"E31.0")}),-1.0]])]});
            var Q1;
            Q1=makeQuery(id+"F4.imprint","IMPRINT",FACE,{"disambiguationData":[TD([[makeQuery(id+"F4.imprint","IMPRINT",EDGE,{"derivedFrom":sQuery(id+"F4.wireOp",EDGE,"E32.0")}),-1.0]])]});
            var Q2;
            Q2=makeQuery(id+"F4.imprint","IMPRINT",FACE,{"disambiguationData":[TD([[makeQuery(id+"F4.imprint","IMPRINT",EDGE,{"derivedFrom":sQuery(id+"F4.wireOp",EDGE,"E33.0")}),-1.0]])]});
            var Q3;
            Q3=makeQuery(id+"F4.imprint","IMPRINT",FACE,{"disambiguationData":[TD([[makeQuery(id+"F4.imprint","IMPRINT",EDGE,{"derivedFrom":sQuery(id+"F4.wireOp",EDGE,"E30.0")}),-1.0]])]});
            extrude(context, id + "F5", {"entities" : qUnion([Q0, Q1, Q2, Q3]), "oppositeDirection" : true, "depth" : 25.4 * mm});
        }
    });
